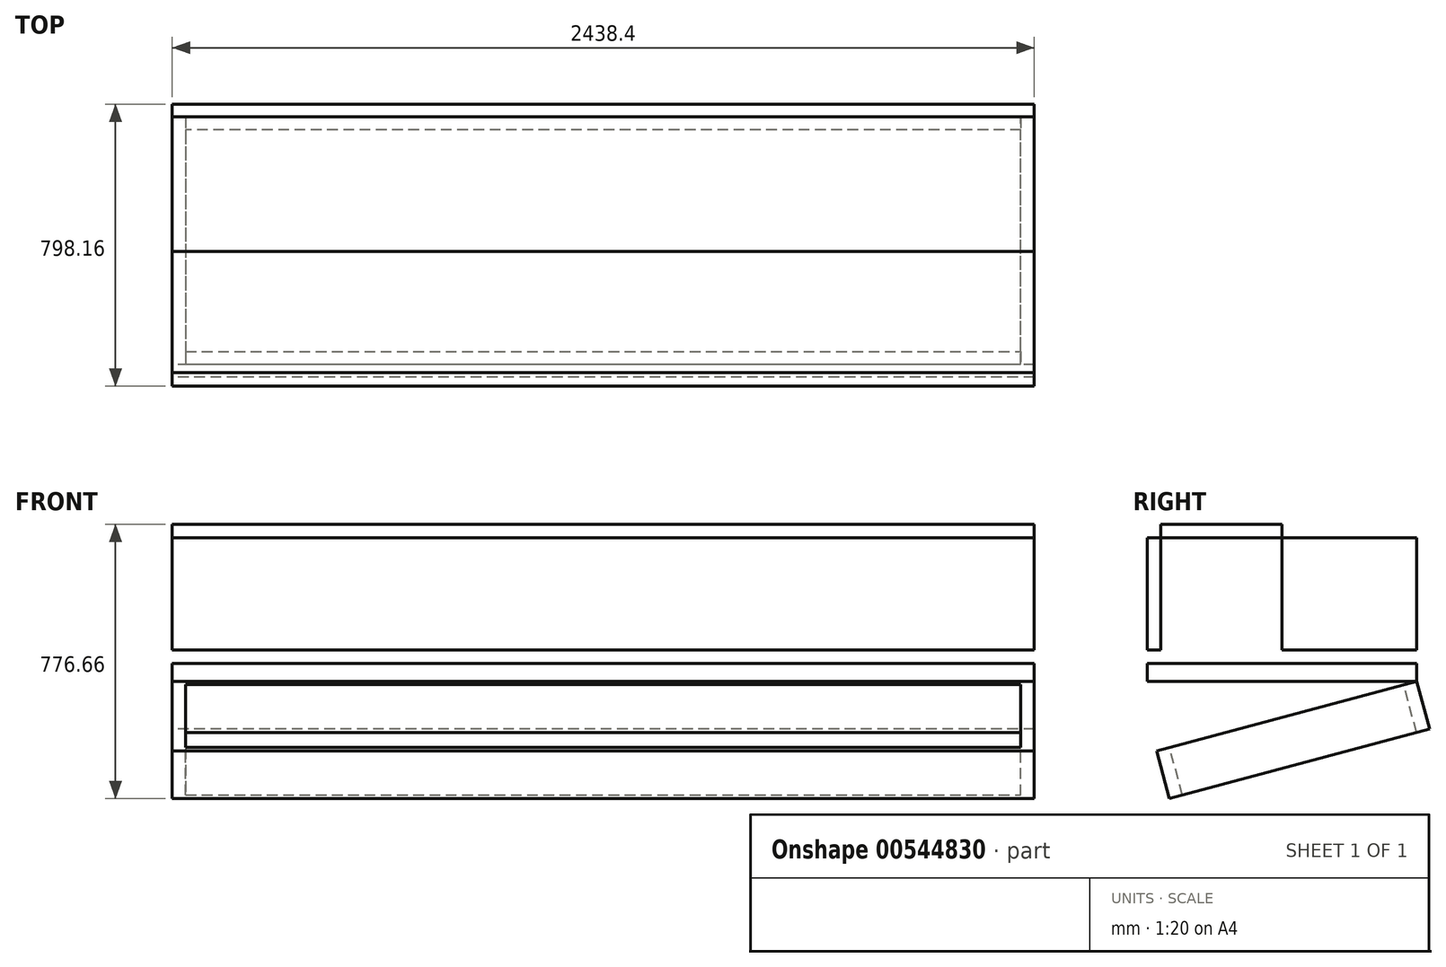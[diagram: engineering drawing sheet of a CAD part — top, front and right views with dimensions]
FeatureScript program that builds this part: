
annotation { "Feature Type Name" : "Feature", "Feature Type Description" : "" }
export const myFeature = defineFeature(function(context is Context, id is Id, definition is map)
    precondition{}
    {
        {
            var Q0;
            Q0=qCreatedBy(makeId("Right.planeOp"),FACE);
            var sketch = newSketch(context, id + "F0", { "sketchPlane" : qUnion([Q0])});
            skLineSegment(sketch, "E0", {"start": v(-950.96, 355.6) * mm, "end": v(-1331.96, 355.6) * mm});
            skLineSegment(sketch, "E1", {"start": v(-1331.96, 355.6) * mm, "end": v(-1712.96, 355.6) * mm});
            skLineSegment(sketch, "E2", {"start": v(-950.96, 355.6) * mm, "end": v(-950.96, -88.9) * mm});
            skLineSegment(sketch, "E3", {"start": v(-950.96, -88.9) * mm, "end": v(-1712.96, -88.9) * mm});
            skLineSegment(sketch, "E4", {"start": v(-1712.96, -88.9) * mm, "end": v(-1712.96, 355.6) * mm});
            skLineSegment(sketch, "E5", {"start": v(-950.96, 0) * mm, "end": v(-1712.96, 0) * mm});
            skLineSegment(sketch, "E6", {"start": v(1870.64, -939.02) * mm, "end": v(-1786.96, -939.02) * mm});
            skLineSegment(sketch, "E7", {"start": v(-1786.96, -939.02) * mm, "end": v(-1786.96, -2158.22) * mm});
            skLineSegment(sketch, "E8", {"start": v(-1786.96, -2158.22) * mm, "end": v(1870.64, -2158.22) * mm});
            skLineSegment(sketch, "E9", {"start": v(1870.64, -2158.22) * mm, "end": v(1870.64, -939.02) * mm});
            skLineSegment(sketch, "E10", {"start": v(1870.64, -1477.83) * mm, "end": v(-1786.96, -1477.83) * mm});
            skLineSegment(sketch, "E11", {"start": v(41.84, -939.02) * mm, "end": v(41.84, -2158.22) * mm});
            skLineSegment(sketch, "E12", {"start": v(1369.93, -1833.43) * mm, "end": v(1045.14, -2158.22) * mm});
            skLineSegment(sketch, "E13", {"start": v(544.43, -2158.22) * mm, "end": v(544.43, -1833.43) * mm});
            skLineSegment(sketch, "E14", {"start": v(1369.93, -1833.43) * mm, "end": v(1870.64, -1833.43) * mm});
            skLineSegment(sketch, "E15", {"start": v(1045.14, -2158.22) * mm, "end": v(544.43, -2158.22) * mm});
            skLineSegment(sketch, "E16", {"start": v(-950.96, -88.9) * mm, "end": v(-1687, -286.12) * mm});
            skLineSegment(sketch, "E17", {"start": v(-1687, -286.12) * mm, "end": v(-1650.84, -421.06) * mm});
            skLineSegment(sketch, "E18", {"start": v(-1650.84, -421.06) * mm, "end": v(-914.8, -223.84) * mm});
            skLineSegment(sketch, "E19", {"start": v(-914.8, -223.84) * mm, "end": v(-950.96, -88.9) * mm});
            skLineSegment(sketch, "E20", {"start": v(132.62, -1901.95) * mm, "end": v(188.83, -1833.43) * mm});
            skLineSegment(sketch, "E21", {"start": v(544.43, -1833.43) * mm, "end": v(544.43, -1901.95) * mm});
            skLineSegment(sketch, "E22", {"start": v(544.43, -1901.95) * mm, "end": v(544.43, -1970.47) * mm});
            skLineSegment(sketch, "E23", {"start": v(188.83, -1901.95) * mm, "end": v(132.62, -1970.47) * mm});
            skLineSegment(sketch, "E24", {"start": v(544.43, -1833.43) * mm, "end": v(188.83, -1833.43) * mm});
            skLineSegment(sketch, "E25", {"start": v(188.83, -1901.95) * mm, "end": v(544.43, -1901.95) * mm});
            skLineSegment(sketch, "E26", {"start": v(1369.93, -1833.43) * mm, "end": v(544.43, -1833.43) * mm});
            skLineSegment(sketch, "E27", {"start": v(188.83, -1833.43) * mm, "end": v(41.84, -1833.43) * mm});
            skLineSegment(sketch, "E28", {"start": v(-1786.96, -1833.43) * mm, "end": v(41.84, -1833.43) * mm});
            skLineSegment(sketch, "E29", {"start": v(544.43, -1970.47) * mm, "end": v(132.62, -1970.47) * mm});
            skLineSegment(sketch, "E30", {"start": v(132.62, -1970.47) * mm, "end": v(41.84, -1970.47) * mm});
            skLineSegment(sketch, "E31", {"start": v(544.43, -1901.95) * mm, "end": v(132.62, -1901.95) * mm});
            skLineSegment(sketch, "E32", {"start": v(132.62, -1901.95) * mm, "end": v(41.84, -1901.95) * mm});
            skLineSegment(sketch, "E33.bottom", {"start": v(-1712.96, 355.6) * mm, "end": v(-1674.86, 355.6) * mm});
            skLineSegment(sketch, "E33.top", {"start": v(-1712.96, 317.5) * mm, "end": v(-1674.86, 317.5) * mm});
            skLineSegment(sketch, "E33.left", {"start": v(-1712.96, 355.6) * mm, "end": v(-1712.96, 317.5) * mm});
            skLineSegment(sketch, "E33.right", {"start": v(-1674.86, 355.6) * mm, "end": v(-1674.86, 317.5) * mm});
            skLineSegment(sketch, "E34.bottom", {"start": v(-950.96, 355.6) * mm, "end": v(-989.06, 355.6) * mm});
            skLineSegment(sketch, "E34.top", {"start": v(-950.96, 317.5) * mm, "end": v(-989.06, 317.5) * mm});
            skLineSegment(sketch, "E34.left", {"start": v(-950.96, 355.6) * mm, "end": v(-950.96, 317.5) * mm});
            skLineSegment(sketch, "E34.right", {"start": v(-989.06, 355.6) * mm, "end": v(-989.06, 317.5) * mm});
            skLineSegment(sketch, "E35", {"start": v(-989.06, 317.5) * mm, "end": v(-989.06, 0) * mm});
            skLineSegment(sketch, "E36", {"start": v(-1674.86, 317.5) * mm, "end": v(-1674.86, 0) * mm});
            skLineSegment(sketch, "E37", {"start": v(-1674.86, 317.5) * mm, "end": v(-989.06, 317.5) * mm});
            skLineSegment(sketch, "E38.bottom", {"start": v(691.26, -2434.24) * mm, "end": v(107.06, -2434.24) * mm});
            skLineSegment(sketch, "E38.top", {"start": v(691.26, -4263.04) * mm, "end": v(107.06, -4263.04) * mm});
            skLineSegment(sketch, "E38.left", {"start": v(691.26, -2434.24) * mm, "end": v(691.26, -4263.04) * mm});
            skLineSegment(sketch, "E38.right", {"start": v(107.06, -2434.24) * mm, "end": v(107.06, -4263.04) * mm});
            skLineSegment(sketch, "E39.bottom", {"start": v(107.06, -2434.24) * mm, "end": v(-286.64, -2434.24) * mm});
            skLineSegment(sketch, "E39.top", {"start": v(107.06, -4263.04) * mm, "end": v(-286.64, -4263.04) * mm});
            skLineSegment(sketch, "E39.right", {"start": v(-286.64, -2434.24) * mm, "end": v(-286.64, -4263.04) * mm});
            skLineSegment(sketch, "E40.bottom", {"start": v(691.26, -2434.24) * mm, "end": v(-527.94, -2434.24) * mm});
            skLineSegment(sketch, "E40.top", {"start": v(691.26, -4872.64) * mm, "end": v(-527.94, -4872.64) * mm});
            skLineSegment(sketch, "E40.left", {"start": v(691.26, -2434.24) * mm, "end": v(691.26, -4872.64) * mm});
            skLineSegment(sketch, "E40.right", {"start": v(-527.94, -2434.24) * mm, "end": v(-527.94, -4872.64) * mm});
            skLineSegment(sketch, "E41", {"start": v(-527.94, -4263.04) * mm, "end": v(246.76, -4263.04) * mm});
            skLineSegment(sketch, "E42", {"start": v(246.76, -4263.04) * mm, "end": v(-134.24, -4644.04) * mm});
            skLineSegment(sketch, "E43", {"start": v(-134.24, -4644.04) * mm, "end": v(-527.94, -4644.04) * mm});
            skLineSegment(sketch, "E44", {"start": v(-950.96, 355.6) * mm, "end": v(-1331.96, 736.6) * mm});
            skLineSegment(sketch, "E45", {"start": v(-1331.96, 736.6) * mm, "end": v(-1712.96, 355.6) * mm});
            skLineSegment(sketch, "E46", {"start": v(-1305.02, 709.66) * mm, "end": v(-1331.96, 682.72) * mm});
            skLineSegment(sketch, "E47", {"start": v(-1331.96, 682.72) * mm, "end": v(-1358.9, 709.66) * mm});
            skLineSegment(sketch, "E48", {"start": v(-1331.96, 682.72) * mm, "end": v(-1004.84, 355.6) * mm});
            skLineSegment(sketch, "E49", {"start": v(-1331.96, 682.72) * mm, "end": v(-1659.08, 355.6) * mm});
            skLineSegment(sketch, "E50", {"start": v(-1331.96, 736.6) * mm, "end": v(-918.87, 323.5) * mm});
            skLineSegment(sketch, "E51", {"start": v(-134.24, -4644.04) * mm, "end": v(640.46, -4644.04) * mm});
            skLineSegment(sketch, "E52", {"start": v(640.46, -4644.04) * mm, "end": v(640.46, -4263.04) * mm});
            skLineSegment(sketch, "E53", {"start": v(640.46, -4263.04) * mm, "end": v(246.76, -4263.04) * mm});
            skLineSegment(sketch, "E54", {"start": v(-1331.96, 736.6) * mm, "end": v(-1331.96, -38.1) * mm});
            skPoint(sketch, "E54.endSnap0", {"position": v(-1331.96, 0) * mm});
            skLineSegment(sketch, "E55", {"start": v(-1331.96, -38.1) * mm, "end": v(-950.96, -38.1) * mm});
            skLineSegment(sketch, "E56", {"start": v(-1331.96, -38.1) * mm, "end": v(-1712.96, -38.1) * mm});
            skLineSegment(sketch, "E57.top", {"start": v(-2269.18, -3223.02) * mm, "end": v(-1507.18, -3223.02) * mm});
            skLineSegment(sketch, "E57.left", {"start": v(-2269.18, -2829.32) * mm, "end": v(-2269.18, -3223.02) * mm});
            skLineSegment(sketch, "E57.right", {"start": v(-1507.18, -2829.32) * mm, "end": v(-1507.18, -3223.02) * mm});
            skLineSegment(sketch, "E58", {"start": v(-2269.18, -2829.32) * mm, "end": v(-1888.18, -2448.32) * mm});
            skLineSegment(sketch, "E59", {"start": v(-1888.18, -2448.32) * mm, "end": v(-1507.18, -2829.32) * mm});
            skLineSegment(sketch, "E60", {"start": v(-2269.18, -2829.32) * mm, "end": v(-1507.18, -2829.32) * mm});
            skSolve(sketch);
        }
        {
            var Q0;
            Q0=makeQuery(id+"F0.imprint","IMPRINT",FACE,{"disambiguationData":[TD([[makeQuery(id+"F0.imprint","IMPRINT",EDGE,{"derivedFrom":sQuery(id+"F0.wireOp",EDGE,"E16")}),1.0]])]});
            extrude(context, id + "F1", {"entities" : qUnion([Q0]), "depth" : 2438.4 * mm, "offsetDistance" : 25.4 * mm});
        }
        {
            var Q0;
            Q0=makeQuery(id+"F1.opExtrude","SWEPT_FACE",FACE,{"disambiguationData":[OSD([sQuery(id+"F0.wireOp",EDGE,"E16")])]});
            var sketch = newSketch(context, id + "F2", { "sketchPlane" : qUnion([Q0])});
            skLineSegment(sketch, "E61", {"start": v(38.1, -1665.47) * mm, "end": v(2400.3, -1665.47) * mm});
            skLineSegment(sketch, "E62", {"start": v(2400.3, -1665.47) * mm, "end": v(2400.3, -979.67) * mm});
            skLineSegment(sketch, "E63", {"start": v(2400.3, -979.67) * mm, "end": v(38.1, -979.67) * mm});
            skLineSegment(sketch, "E64", {"start": v(38.1, -979.67) * mm, "end": v(38.1, -1665.47) * mm});
            skSolve(sketch);
        }
        {
            var Q0;
            Q0=makeQuery(id+"F2.imprint","IMPRINT",FACE,{"disambiguationData":[TD([[makeQuery(id+"F2.imprint","IMPRINT",EDGE,{"derivedFrom":sQuery(id+"F2.wireOp",EDGE,"E61")}),1.0]])]});
            extrude(context, id + "F3", {"entities" : qUnion([Q0]), "operationType" : NewBodyOperationType.REMOVE, "oppositeDirection" : true, "depth" : 203.2 * mm, "offsetDistance" : 25.4 * mm});
        }
        {
            var Q0;
            {var subQ5=sQuery(id+"F0.wireOp",EDGE,"E3");Q0=makeQuery(id+"F0.imprint","IMPRINT",FACE,{"disambiguationData":[TD([[makeQuery(id+"F0.imprint","IMPRINT",EDGE,{"derivedFrom":subQ5}),-1.0]])]});}
            var Q1;
            {var subQ0=sQuery(id+"F0.wireOp",EDGE,"E35");Q1=makeQuery(id+"F0.imprint","IMPRINT",FACE,{"disambiguationData":[TD([[makeQuery(id+"F0.imprint","IMPRINT",EDGE,{"derivedFrom":subQ0}),-1.0]])]});}
            var Q2;
            {var subQ0=sQuery(id+"F0.wireOp",EDGE,"E33.top");Q2=makeQuery(id+"F0.imprint","IMPRINT",FACE,{"disambiguationData":[TD([[makeQuery(id+"F0.imprint","IMPRINT",EDGE,{"derivedFrom":subQ0}),-1.0]])]});}
            var Q3;
            Q3=makeQuery(id+"F0.imprint","IMPRINT",FACE,{"disambiguationData":[TD([[makeQuery(id+"F0.imprint","IMPRINT",EDGE,{"derivedFrom":sQuery(id+"F0.wireOp",EDGE,"E33.bottom")}),-1.0]])]});
            var Q4;
            {var subQ0=sQuery(id+"F0.wireOp",EDGE,"E33.right");Q4=makeQuery(id+"F0.imprint","IMPRINT",FACE,{"disambiguationData":[TD([[makeQuery(id+"F0.imprint","IMPRINT",EDGE,{"derivedFrom":subQ0}),1.0]])]});}
            var Q5;
            {var subQ0=sQuery(id+"F0.wireOp",EDGE,"E34.top");Q5=makeQuery(id+"F0.imprint","IMPRINT",FACE,{"disambiguationData":[TD([[makeQuery(id+"F0.imprint","IMPRINT",EDGE,{"derivedFrom":subQ0}),1.0]])]});}
            var Q6;
            Q6=makeQuery(id+"F0.imprint","IMPRINT",FACE,{"disambiguationData":[TD([[makeQuery(id+"F0.imprint","IMPRINT",EDGE,{"derivedFrom":sQuery(id+"F0.wireOp",EDGE,"E34.bottom")}),1.0]])]});
            var Q7;
            {var subQ0=sQuery(id+"F0.wireOp",EDGE,"E34.bottom");Q7=makeQuery(id+"F0.imprint","IMPRINT",FACE,{"disambiguationData":[TD([[makeQuery(id+"F0.imprint","IMPRINT",EDGE,{"derivedFrom":subQ0}),-1.0]])]});}
            var Q8;
            Q8=makeQuery(id+"F0.imprint","IMPRINT",FACE,{"disambiguationData":[TD([[makeQuery(id+"F0.imprint","IMPRINT",EDGE,{"derivedFrom":sQuery(id+"F0.wireOp",EDGE,"azsKoeuh-ZyM4-USp2-IKpX-wLDT6Y7FB6cZ")}),-1.0]])]});
            var Q9;
            {var subQ0=sQuery(id+"F0.wireOp",EDGE,"E33.bottom");Q9=makeQuery(id+"F0.imprint","IMPRINT",FACE,{"disambiguationData":[TD([[makeQuery(id+"F0.imprint","IMPRINT",EDGE,{"derivedFrom":subQ0}),1.0]])]});}
            var Q10;
            {var subQ3=sQuery(id+"F0.wireOp",EDGE,"sVsZu5uD-f15x-dKsG-83Yc-TrZDROHG2Jsh");Q10=makeQuery(id+"F0.imprint","IMPRINT",FACE,{"disambiguationData":[TD([[makeQuery(id+"F0.imprint","IMPRINT",EDGE,{"derivedFrom":subQ3}),-1.0]])]});}
            extrude(context, id + "F4", {"entities" : qUnion([Q0, Q1, Q2, Q3, Q4, Q5, Q6, Q7, Q8, Q9, Q10]), "depth" : 2438.4 * mm, "offsetDistance" : 25.4 * mm});
        }
    });
